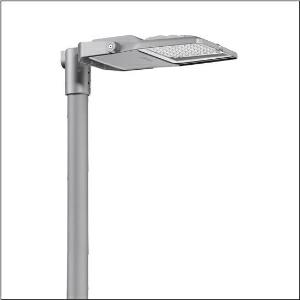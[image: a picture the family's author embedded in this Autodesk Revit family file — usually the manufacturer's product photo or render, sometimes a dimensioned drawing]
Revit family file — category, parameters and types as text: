
# Revit family: floodlight_fl_21_iq_mini___pl64_5xa7772b4e3a_29df
name_source: partatom
category: Lighting Fixtures
units: mm (PartAtom-declared; Revit-internal decimal feet)

## family parameters
Cut with Voids When Loaded = No
Host = Face
Light Source = No
Part Type = Normal
Room Calculation Point = No
Round Connector Dimension = Use Diameter
Shared = No

## types (1)
- --- (1 x LED, 6270 lm, 45.5 W, 4000K)
    Apparent Load = 46 VA
    CIE Flux Codes = 28 80 98 100 100
    Color Rendering = 70
    Color Temperature = 4000K
    Default Elevation = 1800 mm
    Description = Floodlight FL 21 iQ mini, floodlight, primary light control with lens, of PMMA, primary optical cover: protective disc, of toughened safety glass, transparent, light distribution: PL64, light emission: direct distribution, installation type: surface-mounted, LED, High Power LED, rated luminous flux: 6.270lm, luminous efficacy: 138lm/W, light colour: 740, colour temperature: 4000K, control: Auto-Match, Temp-Guard, Night-Set, Smart-Wire, Desk-Remote (wireless, voltage-free reading and setting of iQ features in the workshop via application-optimized NFC function/RFID function), optimised constant luminous flux control (CLO 2.0), Light-Fading, Lumen-Switch, with terminal, 6-pole, mains connection: 220..240V, AC, 50/60Hz, start of lifetime: 46W, end of service life: 48W, reduction: 22W, luminaire housing, of diecast aluminium, powder-coated, Siteco® metallic grey (DB 702S), corrosivity category C5 mid according to DIN EN ISO 12944, sealing non-destructively replaceable, please order mast flange separately, mast bracket, of steel, galvanised, powder-coated, protection rating (complete): IP66, insulation class (complete): insulation class II (safety insulation), certification: CE, ENEC, VDE, protection symbol: D, impact resistance: IK08, permissible operating ambient temperature: -40..+40°C, permissible operating ambient temperature for outdoor applications: -40..+50°C, standard: DIN EN 12944, LABS conformity tested according to VDMA 24364:2018-05, packaging unit: 1 piece

Light Distribution: PL64
    Height = 70 mm
    Lamp = 1 x LED
    Lamp Light Flux = 6270 lm
    Lamp Power = 45.5 W
    Lamp count = 1
    Length = 485 mm
    Luminous efficacy = 138 lm/W
    Manufacturer = Siteco
    ModVariant = No
    Model = 5XA7772B4E3A
    Number of Poles = 1
    OnlyDefault = Yes
    Power Factor = 1
    Product Name = Floodlight FL 21 iQ mini | PL64
    Product group = floodlight | pylon annexe
    ProductGroupID = 6200
    Protection Class = Protection class II
    Protection Degree = IP 66
    RLX_Detail_Level = 1
    RLX_Emergency_Light_Flux = 0 lm
    RLX_Emergency_Type = 0
    RLX_Emergency_Type_DB = No
    RlxData = <blob elided: 101245 chars, md5=9538b698>
    Socket = socket
    Standby Power = 0 W
    System Light Flux = 6270 lm
    System Power = 46 W
    Type Comments = factory setting: luminous flux: 100 % | dim-lin: 254 | 463 mA
    Type Image = l_1007125.jpg
    URL = http://relux.com
    VarID = @adj_116909
    Voltage = 0 V
    Weight = 0.00 kg
    Width = 337 mm

## geometry (parser evidence)
native form markers: Blend x4, Sweep x13
no freeform markers — native parametric forms only
